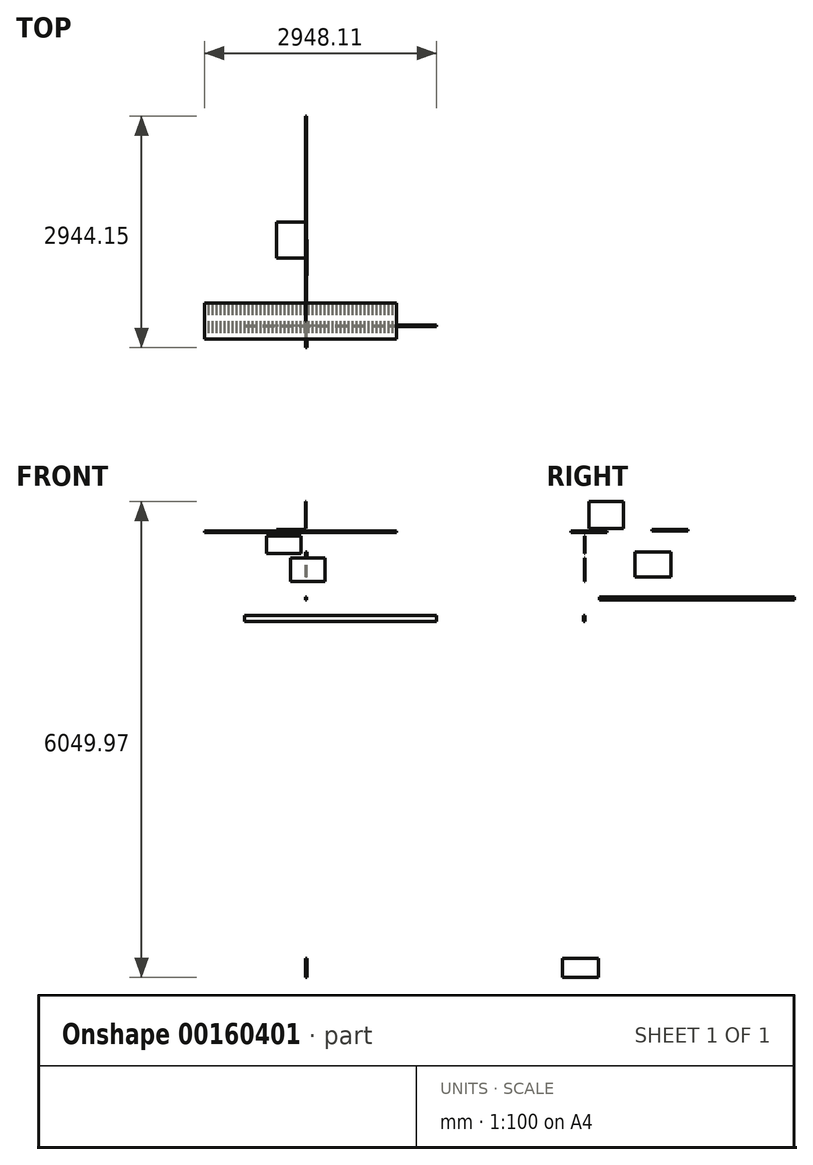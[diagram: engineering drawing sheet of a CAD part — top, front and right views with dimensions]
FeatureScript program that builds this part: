
annotation { "Feature Type Name" : "Feature", "Feature Type Description" : "" }
export const myFeature = defineFeature(function(context is Context, id is Id, definition is map)
    precondition{}
    {
        {
            var Q0;
            Q0=qCreatedBy(makeId("Top.planeOp"),FACE);
            var sketch = newSketch(context, id + "F0", { "sketchPlane" : qUnion([Q0])});
            skLineSegment(sketch, "E0.bottom", {"start": v(-1285.12, 279.2) * mm, "end": v(1153.28, 279.2) * mm});
            skLineSegment(sketch, "E0.top", {"start": v(-1285.12, -178) * mm, "end": v(1153.28, -178) * mm});
            skLineSegment(sketch, "E0.left", {"start": v(-1285.12, 279.2) * mm, "end": v(-1285.12, -178) * mm});
            skLineSegment(sketch, "E0.right", {"start": v(1153.28, 279.2) * mm, "end": v(1153.28, -178) * mm});
            skLineSegment(sketch, "E1.0", {"start": v(-1237.5, 279.2) * mm, "end": v(-1237.5, -178) * mm});
            skLineSegment(sketch, "E2.0", {"start": v(-1231.15, 279.2) * mm, "end": v(-1231.15, -178) * mm});
            skLineSegment(sketch, "E3.1.0.0", {"start": v(-1180.35, 279.2) * mm, "end": v(-1180.35, -178) * mm});
            skLineSegment(sketch, "E3.1.0.1", {"start": v(-1186.7, 279.2) * mm, "end": v(-1186.7, -178) * mm});
            skLineSegment(sketch, "E3.2.0.0", {"start": v(-1129.55, 279.2) * mm, "end": v(-1129.55, -178) * mm});
            skLineSegment(sketch, "E3.2.0.1", {"start": v(-1135.9, 279.2) * mm, "end": v(-1135.9, -178) * mm});
            skLineSegment(sketch, "E3.3.0.0", {"start": v(-1078.75, 279.2) * mm, "end": v(-1078.75, -178) * mm});
            skLineSegment(sketch, "E3.3.0.1", {"start": v(-1085.1, 279.2) * mm, "end": v(-1085.1, -178) * mm});
            skLineSegment(sketch, "E3.4.0.0", {"start": v(-1027.95, 279.2) * mm, "end": v(-1027.95, -178) * mm});
            skLineSegment(sketch, "E3.4.0.1", {"start": v(-1034.3, 279.2) * mm, "end": v(-1034.3, -178) * mm});
            skLineSegment(sketch, "E3.5.0.0", {"start": v(-977.15, 279.2) * mm, "end": v(-977.15, -178) * mm});
            skLineSegment(sketch, "E3.5.0.1", {"start": v(-983.5, 279.2) * mm, "end": v(-983.5, -178) * mm});
            skLineSegment(sketch, "E3.6.0.0", {"start": v(-926.35, 279.2) * mm, "end": v(-926.35, -178) * mm});
            skLineSegment(sketch, "E3.6.0.1", {"start": v(-932.7, 279.2) * mm, "end": v(-932.7, -178) * mm});
            skLineSegment(sketch, "E3.7.0.0", {"start": v(-875.55, 279.2) * mm, "end": v(-875.55, -178) * mm});
            skLineSegment(sketch, "E3.7.0.1", {"start": v(-881.9, 279.2) * mm, "end": v(-881.9, -178) * mm});
            skLineSegment(sketch, "E3.8.0.0", {"start": v(-824.75, 279.2) * mm, "end": v(-824.75, -178) * mm});
            skLineSegment(sketch, "E3.8.0.1", {"start": v(-831.1, 279.2) * mm, "end": v(-831.1, -178) * mm});
            skLineSegment(sketch, "E3.9.0.0", {"start": v(-773.95, 279.2) * mm, "end": v(-773.95, -178) * mm});
            skLineSegment(sketch, "E3.9.0.1", {"start": v(-780.3, 279.2) * mm, "end": v(-780.3, -178) * mm});
            skLineSegment(sketch, "E3.10.0.0", {"start": v(-723.15, 279.2) * mm, "end": v(-723.15, -178) * mm});
            skLineSegment(sketch, "E3.10.0.1", {"start": v(-729.5, 279.2) * mm, "end": v(-729.5, -178) * mm});
            skLineSegment(sketch, "E3.11.0.0", {"start": v(-672.35, 279.2) * mm, "end": v(-672.35, -178) * mm});
            skLineSegment(sketch, "E3.11.0.1", {"start": v(-678.7, 279.2) * mm, "end": v(-678.7, -178) * mm});
            skLineSegment(sketch, "E3.12.0.0", {"start": v(-621.55, 279.2) * mm, "end": v(-621.55, -178) * mm});
            skLineSegment(sketch, "E3.12.0.1", {"start": v(-627.9, 279.2) * mm, "end": v(-627.9, -178) * mm});
            skLineSegment(sketch, "E3.13.0.0", {"start": v(-570.75, 279.2) * mm, "end": v(-570.75, -178) * mm});
            skLineSegment(sketch, "E3.13.0.1", {"start": v(-577.1, 279.2) * mm, "end": v(-577.1, -178) * mm});
            skLineSegment(sketch, "E3.14.0.0", {"start": v(-519.95, 279.2) * mm, "end": v(-519.95, -178) * mm});
            skLineSegment(sketch, "E3.14.0.1", {"start": v(-526.3, 279.2) * mm, "end": v(-526.3, -178) * mm});
            skLineSegment(sketch, "E3.15.0.0", {"start": v(-469.15, 279.2) * mm, "end": v(-469.15, -178) * mm});
            skLineSegment(sketch, "E3.15.0.1", {"start": v(-475.5, 279.2) * mm, "end": v(-475.5, -178) * mm});
            skLineSegment(sketch, "E3.16.0.0", {"start": v(-418.35, 279.2) * mm, "end": v(-418.35, -178) * mm});
            skLineSegment(sketch, "E3.16.0.1", {"start": v(-424.7, 279.2) * mm, "end": v(-424.7, -178) * mm});
            skLineSegment(sketch, "E3.17.0.0", {"start": v(-367.55, 279.2) * mm, "end": v(-367.55, -178) * mm});
            skLineSegment(sketch, "E3.17.0.1", {"start": v(-373.9, 279.2) * mm, "end": v(-373.9, -178) * mm});
            skLineSegment(sketch, "E3.18.0.0", {"start": v(-316.75, 279.2) * mm, "end": v(-316.75, -178) * mm});
            skLineSegment(sketch, "E3.18.0.1", {"start": v(-323.1, 279.2) * mm, "end": v(-323.1, -178) * mm});
            skLineSegment(sketch, "E3.19.0.0", {"start": v(-265.95, 279.2) * mm, "end": v(-265.95, -178) * mm});
            skLineSegment(sketch, "E3.19.0.1", {"start": v(-272.3, 279.2) * mm, "end": v(-272.3, -178) * mm});
            skLineSegment(sketch, "E3.20.0.0", {"start": v(-215.15, 279.2) * mm, "end": v(-215.15, -178) * mm});
            skLineSegment(sketch, "E3.20.0.1", {"start": v(-221.5, 279.2) * mm, "end": v(-221.5, -178) * mm});
            skLineSegment(sketch, "E3.21.0.0", {"start": v(-164.35, 279.2) * mm, "end": v(-164.35, -178) * mm});
            skLineSegment(sketch, "E3.21.0.1", {"start": v(-170.7, 279.2) * mm, "end": v(-170.7, -178) * mm});
            skLineSegment(sketch, "E3.22.0.0", {"start": v(-113.55, 279.2) * mm, "end": v(-113.55, -178) * mm});
            skLineSegment(sketch, "E3.22.0.1", {"start": v(-119.9, 279.2) * mm, "end": v(-119.9, -178) * mm});
            skLineSegment(sketch, "E3.23.0.0", {"start": v(-62.75, 279.2) * mm, "end": v(-62.75, -178) * mm});
            skLineSegment(sketch, "E3.23.0.1", {"start": v(-69.1, 279.2) * mm, "end": v(-69.1, -178) * mm});
            skLineSegment(sketch, "E3.24.0.0", {"start": v(-11.95, 279.2) * mm, "end": v(-11.95, -178) * mm});
            skLineSegment(sketch, "E3.24.0.1", {"start": v(-18.3, 279.2) * mm, "end": v(-18.3, -178) * mm});
            skLineSegment(sketch, "E3.25.0.0", {"start": v(38.85, 279.2) * mm, "end": v(38.85, -178) * mm});
            skLineSegment(sketch, "E3.25.0.1", {"start": v(32.5, 279.2) * mm, "end": v(32.5, -178) * mm});
            skLineSegment(sketch, "E3.26.0.0", {"start": v(89.65, 279.2) * mm, "end": v(89.65, -178) * mm});
            skLineSegment(sketch, "E3.26.0.1", {"start": v(83.3, 279.2) * mm, "end": v(83.3, -178) * mm});
            skLineSegment(sketch, "E3.27.0.0", {"start": v(140.45, 279.2) * mm, "end": v(140.45, -178) * mm});
            skLineSegment(sketch, "E3.27.0.1", {"start": v(134.1, 279.2) * mm, "end": v(134.1, -178) * mm});
            skLineSegment(sketch, "E3.28.0.0", {"start": v(191.25, 279.2) * mm, "end": v(191.25, -178) * mm});
            skLineSegment(sketch, "E3.28.0.1", {"start": v(184.9, 279.2) * mm, "end": v(184.9, -178) * mm});
            skLineSegment(sketch, "E3.29.0.0", {"start": v(242.05, 279.2) * mm, "end": v(242.05, -178) * mm});
            skLineSegment(sketch, "E3.29.0.1", {"start": v(235.7, 279.2) * mm, "end": v(235.7, -178) * mm});
            skLineSegment(sketch, "E3.30.0.0", {"start": v(292.85, 279.2) * mm, "end": v(292.85, -178) * mm});
            skLineSegment(sketch, "E3.30.0.1", {"start": v(286.5, 279.2) * mm, "end": v(286.5, -178) * mm});
            skLineSegment(sketch, "E3.31.0.0", {"start": v(343.65, 279.2) * mm, "end": v(343.65, -178) * mm});
            skLineSegment(sketch, "E3.31.0.1", {"start": v(337.3, 279.2) * mm, "end": v(337.3, -178) * mm});
            skLineSegment(sketch, "E3.32.0.0", {"start": v(394.45, 279.2) * mm, "end": v(394.45, -178) * mm});
            skLineSegment(sketch, "E3.32.0.1", {"start": v(388.1, 279.2) * mm, "end": v(388.1, -178) * mm});
            skLineSegment(sketch, "E3.33.0.0", {"start": v(445.25, 279.2) * mm, "end": v(445.25, -178) * mm});
            skLineSegment(sketch, "E3.33.0.1", {"start": v(438.9, 279.2) * mm, "end": v(438.9, -178) * mm});
            skLineSegment(sketch, "E3.34.0.0", {"start": v(496.05, 279.2) * mm, "end": v(496.05, -178) * mm});
            skLineSegment(sketch, "E3.34.0.1", {"start": v(489.7, 279.2) * mm, "end": v(489.7, -178) * mm});
            skLineSegment(sketch, "E3.35.0.0", {"start": v(546.85, 279.2) * mm, "end": v(546.85, -178) * mm});
            skLineSegment(sketch, "E3.35.0.1", {"start": v(540.5, 279.2) * mm, "end": v(540.5, -178) * mm});
            skLineSegment(sketch, "E3.36.0.0", {"start": v(597.65, 279.2) * mm, "end": v(597.65, -178) * mm});
            skLineSegment(sketch, "E3.36.0.1", {"start": v(591.3, 279.2) * mm, "end": v(591.3, -178) * mm});
            skLineSegment(sketch, "E3.37.0.0", {"start": v(648.45, 279.2) * mm, "end": v(648.45, -178) * mm});
            skLineSegment(sketch, "E3.37.0.1", {"start": v(642.1, 279.2) * mm, "end": v(642.1, -178) * mm});
            skLineSegment(sketch, "E3.38.0.0", {"start": v(699.25, 279.2) * mm, "end": v(699.25, -178) * mm});
            skLineSegment(sketch, "E3.38.0.1", {"start": v(692.9, 279.2) * mm, "end": v(692.9, -178) * mm});
            skLineSegment(sketch, "E3.39.0.0", {"start": v(750.05, 279.2) * mm, "end": v(750.05, -178) * mm});
            skLineSegment(sketch, "E3.39.0.1", {"start": v(743.7, 279.2) * mm, "end": v(743.7, -178) * mm});
            skLineSegment(sketch, "E3.40.0.0", {"start": v(800.85, 279.2) * mm, "end": v(800.85, -178) * mm});
            skLineSegment(sketch, "E3.40.0.1", {"start": v(794.5, 279.2) * mm, "end": v(794.5, -178) * mm});
            skLineSegment(sketch, "E3.41.0.0", {"start": v(851.65, 279.2) * mm, "end": v(851.65, -178) * mm});
            skLineSegment(sketch, "E3.41.0.1", {"start": v(845.3, 279.2) * mm, "end": v(845.3, -178) * mm});
            skLineSegment(sketch, "E3.42.0.0", {"start": v(902.45, 279.2) * mm, "end": v(902.45, -178) * mm});
            skLineSegment(sketch, "E3.42.0.1", {"start": v(896.1, 279.2) * mm, "end": v(896.1, -178) * mm});
            skLineSegment(sketch, "E3.43.0.0", {"start": v(953.25, 279.2) * mm, "end": v(953.25, -178) * mm});
            skLineSegment(sketch, "E3.43.0.1", {"start": v(946.9, 279.2) * mm, "end": v(946.9, -178) * mm});
            skLineSegment(sketch, "E3.44.0.0", {"start": v(1004.05, 279.2) * mm, "end": v(1004.05, -178) * mm});
            skLineSegment(sketch, "E3.44.0.1", {"start": v(997.7, 279.2) * mm, "end": v(997.7, -178) * mm});
            skLineSegment(sketch, "E3.45.0.0", {"start": v(1054.85, 279.2) * mm, "end": v(1054.85, -178) * mm});
            skLineSegment(sketch, "E3.45.0.1", {"start": v(1048.5, 279.2) * mm, "end": v(1048.5, -178) * mm});
            skLineSegment(sketch, "E3.46.0.0", {"start": v(1105.65, 279.2) * mm, "end": v(1105.65, -178) * mm});
            skLineSegment(sketch, "E3.46.0.1", {"start": v(1099.3, 279.2) * mm, "end": v(1099.3, -178) * mm});
            skLineSegment(sketch, "E3.direction1", {"start": v(-1237.5, -178) * mm, "end": v(-1186.7, -178) * mm, "construction": true});
            skSolve(sketch);
        }
        {
            var Q0;
            Q0 = qSketchRegion(id + "F0", true);
            extrude(context, id + "F1", {"entities" : qUnion([Q0]), "depth" : 19.05 * mm});
        }
        {
            var Q0;
            {var subQ0=sQuery(id+"F0.wireOp",EDGE,"E1.0");Q0=makeQuery(id+"F0.imprint","IMPRINT",FACE,{"disambiguationData":[TD([[makeQuery(id+"F0.imprint","IMPRINT",EDGE,{"derivedFrom":subQ0}),1.0]])]});}
            var Q1;
            {var subQ0=sQuery(id+"F0.wireOp",EDGE,"E3.1.0.0");Q1=makeQuery(id+"F0.imprint","IMPRINT",FACE,{"disambiguationData":[TD([[makeQuery(id+"F0.imprint","IMPRINT",EDGE,{"derivedFrom":subQ0}),-1.0]])]});}
            var Q2;
            {var subQ0=sQuery(id+"F0.wireOp",EDGE,"E3.2.0.0");Q2=makeQuery(id+"F0.imprint","IMPRINT",FACE,{"disambiguationData":[TD([[makeQuery(id+"F0.imprint","IMPRINT",EDGE,{"derivedFrom":subQ0}),-1.0]])]});}
            var Q3;
            {var subQ0=sQuery(id+"F0.wireOp",EDGE,"E3.3.0.0");Q3=makeQuery(id+"F0.imprint","IMPRINT",FACE,{"disambiguationData":[TD([[makeQuery(id+"F0.imprint","IMPRINT",EDGE,{"derivedFrom":subQ0}),-1.0]])]});}
            var Q4;
            {var subQ0=sQuery(id+"F0.wireOp",EDGE,"E3.4.0.0");Q4=makeQuery(id+"F0.imprint","IMPRINT",FACE,{"disambiguationData":[TD([[makeQuery(id+"F0.imprint","IMPRINT",EDGE,{"derivedFrom":subQ0}),-1.0]])]});}
            var Q5;
            {var subQ0=sQuery(id+"F0.wireOp",EDGE,"E3.5.0.0");Q5=makeQuery(id+"F0.imprint","IMPRINT",FACE,{"disambiguationData":[TD([[makeQuery(id+"F0.imprint","IMPRINT",EDGE,{"derivedFrom":subQ0}),-1.0]])]});}
            var Q6;
            {var subQ0=sQuery(id+"F0.wireOp",EDGE,"E3.6.0.0");Q6=makeQuery(id+"F0.imprint","IMPRINT",FACE,{"disambiguationData":[TD([[makeQuery(id+"F0.imprint","IMPRINT",EDGE,{"derivedFrom":subQ0}),-1.0]])]});}
            var Q7;
            {var subQ0=sQuery(id+"F0.wireOp",EDGE,"E3.7.0.0");Q7=makeQuery(id+"F0.imprint","IMPRINT",FACE,{"disambiguationData":[TD([[makeQuery(id+"F0.imprint","IMPRINT",EDGE,{"derivedFrom":subQ0}),-1.0]])]});}
            var Q8;
            {var subQ0=sQuery(id+"F0.wireOp",EDGE,"E3.8.0.0");Q8=makeQuery(id+"F0.imprint","IMPRINT",FACE,{"disambiguationData":[TD([[makeQuery(id+"F0.imprint","IMPRINT",EDGE,{"derivedFrom":subQ0}),-1.0]])]});}
            var Q9;
            {var subQ0=sQuery(id+"F0.wireOp",EDGE,"E3.9.0.0");Q9=makeQuery(id+"F0.imprint","IMPRINT",FACE,{"disambiguationData":[TD([[makeQuery(id+"F0.imprint","IMPRINT",EDGE,{"derivedFrom":subQ0}),-1.0]])]});}
            var Q10;
            {var subQ0=sQuery(id+"F0.wireOp",EDGE,"E3.10.0.0");Q10=makeQuery(id+"F0.imprint","IMPRINT",FACE,{"disambiguationData":[TD([[makeQuery(id+"F0.imprint","IMPRINT",EDGE,{"derivedFrom":subQ0}),-1.0]])]});}
            var Q11;
            {var subQ0=sQuery(id+"F0.wireOp",EDGE,"E3.11.0.0");Q11=makeQuery(id+"F0.imprint","IMPRINT",FACE,{"disambiguationData":[TD([[makeQuery(id+"F0.imprint","IMPRINT",EDGE,{"derivedFrom":subQ0}),-1.0]])]});}
            var Q12;
            {var subQ0=sQuery(id+"F0.wireOp",EDGE,"E3.12.0.0");Q12=makeQuery(id+"F0.imprint","IMPRINT",FACE,{"disambiguationData":[TD([[makeQuery(id+"F0.imprint","IMPRINT",EDGE,{"derivedFrom":subQ0}),-1.0]])]});}
            var Q13;
            {var subQ0=sQuery(id+"F0.wireOp",EDGE,"E3.13.0.0");Q13=makeQuery(id+"F0.imprint","IMPRINT",FACE,{"disambiguationData":[TD([[makeQuery(id+"F0.imprint","IMPRINT",EDGE,{"derivedFrom":subQ0}),-1.0]])]});}
            var Q14;
            {var subQ0=sQuery(id+"F0.wireOp",EDGE,"E3.14.0.0");Q14=makeQuery(id+"F0.imprint","IMPRINT",FACE,{"disambiguationData":[TD([[makeQuery(id+"F0.imprint","IMPRINT",EDGE,{"derivedFrom":subQ0}),-1.0]])]});}
            var Q15;
            {var subQ0=sQuery(id+"F0.wireOp",EDGE,"E3.15.0.0");Q15=makeQuery(id+"F0.imprint","IMPRINT",FACE,{"disambiguationData":[TD([[makeQuery(id+"F0.imprint","IMPRINT",EDGE,{"derivedFrom":subQ0}),-1.0]])]});}
            var Q16;
            {var subQ0=sQuery(id+"F0.wireOp",EDGE,"E3.16.0.0");Q16=makeQuery(id+"F0.imprint","IMPRINT",FACE,{"disambiguationData":[TD([[makeQuery(id+"F0.imprint","IMPRINT",EDGE,{"derivedFrom":subQ0}),-1.0]])]});}
            var Q17;
            {var subQ0=sQuery(id+"F0.wireOp",EDGE,"E3.17.0.0");Q17=makeQuery(id+"F0.imprint","IMPRINT",FACE,{"disambiguationData":[TD([[makeQuery(id+"F0.imprint","IMPRINT",EDGE,{"derivedFrom":subQ0}),-1.0]])]});}
            var Q18;
            {var subQ0=sQuery(id+"F0.wireOp",EDGE,"E3.18.0.0");Q18=makeQuery(id+"F0.imprint","IMPRINT",FACE,{"disambiguationData":[TD([[makeQuery(id+"F0.imprint","IMPRINT",EDGE,{"derivedFrom":subQ0}),-1.0]])]});}
            var Q19;
            {var subQ0=sQuery(id+"F0.wireOp",EDGE,"E3.19.0.0");Q19=makeQuery(id+"F0.imprint","IMPRINT",FACE,{"disambiguationData":[TD([[makeQuery(id+"F0.imprint","IMPRINT",EDGE,{"derivedFrom":subQ0}),-1.0]])]});}
            var Q20;
            {var subQ0=sQuery(id+"F0.wireOp",EDGE,"E3.20.0.0");Q20=makeQuery(id+"F0.imprint","IMPRINT",FACE,{"disambiguationData":[TD([[makeQuery(id+"F0.imprint","IMPRINT",EDGE,{"derivedFrom":subQ0}),-1.0]])]});}
            var Q21;
            {var subQ0=sQuery(id+"F0.wireOp",EDGE,"E3.21.0.0");Q21=makeQuery(id+"F0.imprint","IMPRINT",FACE,{"disambiguationData":[TD([[makeQuery(id+"F0.imprint","IMPRINT",EDGE,{"derivedFrom":subQ0}),-1.0]])]});}
            var Q22;
            {var subQ0=sQuery(id+"F0.wireOp",EDGE,"E3.22.0.0");Q22=makeQuery(id+"F0.imprint","IMPRINT",FACE,{"disambiguationData":[TD([[makeQuery(id+"F0.imprint","IMPRINT",EDGE,{"derivedFrom":subQ0}),-1.0]])]});}
            var Q23;
            {var subQ0=sQuery(id+"F0.wireOp",EDGE,"E3.23.0.0");Q23=makeQuery(id+"F0.imprint","IMPRINT",FACE,{"disambiguationData":[TD([[makeQuery(id+"F0.imprint","IMPRINT",EDGE,{"derivedFrom":subQ0}),-1.0]])]});}
            var Q24;
            {var subQ0=sQuery(id+"F0.wireOp",EDGE,"E3.24.0.0");Q24=makeQuery(id+"F0.imprint","IMPRINT",FACE,{"disambiguationData":[TD([[makeQuery(id+"F0.imprint","IMPRINT",EDGE,{"derivedFrom":subQ0}),-1.0]])]});}
            var Q25;
            {var subQ0=sQuery(id+"F0.wireOp",EDGE,"E3.25.0.0");Q25=makeQuery(id+"F0.imprint","IMPRINT",FACE,{"disambiguationData":[TD([[makeQuery(id+"F0.imprint","IMPRINT",EDGE,{"derivedFrom":subQ0}),-1.0]])]});}
            var Q26;
            {var subQ0=sQuery(id+"F0.wireOp",EDGE,"E3.26.0.0");Q26=makeQuery(id+"F0.imprint","IMPRINT",FACE,{"disambiguationData":[TD([[makeQuery(id+"F0.imprint","IMPRINT",EDGE,{"derivedFrom":subQ0}),-1.0]])]});}
            var Q27;
            {var subQ0=sQuery(id+"F0.wireOp",EDGE,"E3.27.0.0");Q27=makeQuery(id+"F0.imprint","IMPRINT",FACE,{"disambiguationData":[TD([[makeQuery(id+"F0.imprint","IMPRINT",EDGE,{"derivedFrom":subQ0}),-1.0]])]});}
            var Q28;
            {var subQ0=sQuery(id+"F0.wireOp",EDGE,"E3.28.0.0");Q28=makeQuery(id+"F0.imprint","IMPRINT",FACE,{"disambiguationData":[TD([[makeQuery(id+"F0.imprint","IMPRINT",EDGE,{"derivedFrom":subQ0}),-1.0]])]});}
            var Q29;
            {var subQ0=sQuery(id+"F0.wireOp",EDGE,"E3.29.0.0");Q29=makeQuery(id+"F0.imprint","IMPRINT",FACE,{"disambiguationData":[TD([[makeQuery(id+"F0.imprint","IMPRINT",EDGE,{"derivedFrom":subQ0}),-1.0]])]});}
            var Q30;
            {var subQ0=sQuery(id+"F0.wireOp",EDGE,"E3.30.0.0");Q30=makeQuery(id+"F0.imprint","IMPRINT",FACE,{"disambiguationData":[TD([[makeQuery(id+"F0.imprint","IMPRINT",EDGE,{"derivedFrom":subQ0}),-1.0]])]});}
            var Q31;
            {var subQ0=sQuery(id+"F0.wireOp",EDGE,"E3.31.0.0");Q31=makeQuery(id+"F0.imprint","IMPRINT",FACE,{"disambiguationData":[TD([[makeQuery(id+"F0.imprint","IMPRINT",EDGE,{"derivedFrom":subQ0}),-1.0]])]});}
            var Q32;
            {var subQ0=sQuery(id+"F0.wireOp",EDGE,"E3.32.0.0");Q32=makeQuery(id+"F0.imprint","IMPRINT",FACE,{"disambiguationData":[TD([[makeQuery(id+"F0.imprint","IMPRINT",EDGE,{"derivedFrom":subQ0}),-1.0]])]});}
            var Q33;
            {var subQ0=sQuery(id+"F0.wireOp",EDGE,"E3.33.0.0");Q33=makeQuery(id+"F0.imprint","IMPRINT",FACE,{"disambiguationData":[TD([[makeQuery(id+"F0.imprint","IMPRINT",EDGE,{"derivedFrom":subQ0}),-1.0]])]});}
            var Q34;
            {var subQ0=sQuery(id+"F0.wireOp",EDGE,"E3.34.0.0");Q34=makeQuery(id+"F0.imprint","IMPRINT",FACE,{"disambiguationData":[TD([[makeQuery(id+"F0.imprint","IMPRINT",EDGE,{"derivedFrom":subQ0}),-1.0]])]});}
            var Q35;
            {var subQ0=sQuery(id+"F0.wireOp",EDGE,"E3.35.0.0");Q35=makeQuery(id+"F0.imprint","IMPRINT",FACE,{"disambiguationData":[TD([[makeQuery(id+"F0.imprint","IMPRINT",EDGE,{"derivedFrom":subQ0}),-1.0]])]});}
            var Q36;
            {var subQ0=sQuery(id+"F0.wireOp",EDGE,"E3.36.0.0");Q36=makeQuery(id+"F0.imprint","IMPRINT",FACE,{"disambiguationData":[TD([[makeQuery(id+"F0.imprint","IMPRINT",EDGE,{"derivedFrom":subQ0}),-1.0]])]});}
            var Q37;
            {var subQ0=sQuery(id+"F0.wireOp",EDGE,"E3.37.0.0");Q37=makeQuery(id+"F0.imprint","IMPRINT",FACE,{"disambiguationData":[TD([[makeQuery(id+"F0.imprint","IMPRINT",EDGE,{"derivedFrom":subQ0}),-1.0]])]});}
            var Q38;
            {var subQ0=sQuery(id+"F0.wireOp",EDGE,"E3.38.0.0");Q38=makeQuery(id+"F0.imprint","IMPRINT",FACE,{"disambiguationData":[TD([[makeQuery(id+"F0.imprint","IMPRINT",EDGE,{"derivedFrom":subQ0}),-1.0]])]});}
            var Q39;
            {var subQ0=sQuery(id+"F0.wireOp",EDGE,"E3.39.0.0");Q39=makeQuery(id+"F0.imprint","IMPRINT",FACE,{"disambiguationData":[TD([[makeQuery(id+"F0.imprint","IMPRINT",EDGE,{"derivedFrom":subQ0}),-1.0]])]});}
            var Q40;
            {var subQ0=sQuery(id+"F0.wireOp",EDGE,"E3.40.0.0");Q40=makeQuery(id+"F0.imprint","IMPRINT",FACE,{"disambiguationData":[TD([[makeQuery(id+"F0.imprint","IMPRINT",EDGE,{"derivedFrom":subQ0}),-1.0]])]});}
            var Q41;
            {var subQ0=sQuery(id+"F0.wireOp",EDGE,"E3.41.0.0");Q41=makeQuery(id+"F0.imprint","IMPRINT",FACE,{"disambiguationData":[TD([[makeQuery(id+"F0.imprint","IMPRINT",EDGE,{"derivedFrom":subQ0}),-1.0]])]});}
            var Q42;
            {var subQ0=sQuery(id+"F0.wireOp",EDGE,"E3.42.0.0");Q42=makeQuery(id+"F0.imprint","IMPRINT",FACE,{"disambiguationData":[TD([[makeQuery(id+"F0.imprint","IMPRINT",EDGE,{"derivedFrom":subQ0}),-1.0]])]});}
            var Q43;
            {var subQ0=sQuery(id+"F0.wireOp",EDGE,"E3.43.0.0");Q43=makeQuery(id+"F0.imprint","IMPRINT",FACE,{"disambiguationData":[TD([[makeQuery(id+"F0.imprint","IMPRINT",EDGE,{"derivedFrom":subQ0}),-1.0]])]});}
            var Q44;
            {var subQ0=sQuery(id+"F0.wireOp",EDGE,"E3.44.0.0");Q44=makeQuery(id+"F0.imprint","IMPRINT",FACE,{"disambiguationData":[TD([[makeQuery(id+"F0.imprint","IMPRINT",EDGE,{"derivedFrom":subQ0}),-1.0]])]});}
            var Q45;
            {var subQ0=sQuery(id+"F0.wireOp",EDGE,"E3.45.0.0");Q45=makeQuery(id+"F0.imprint","IMPRINT",FACE,{"disambiguationData":[TD([[makeQuery(id+"F0.imprint","IMPRINT",EDGE,{"derivedFrom":subQ0}),-1.0]])]});}
            var Q46;
            {var subQ0=sQuery(id+"F0.wireOp",EDGE,"E3.46.0.0");Q46=makeQuery(id+"F0.imprint","IMPRINT",FACE,{"disambiguationData":[TD([[makeQuery(id+"F0.imprint","IMPRINT",EDGE,{"derivedFrom":subQ0}),-1.0]])]});}
            extrude(context, id + "F2", {"entities" : qUnion([Q0, Q1, Q2, Q3, Q4, Q5, Q6, Q7, Q8, Q9, Q10, Q11, Q12, Q13, Q14, Q15, Q16, Q17, Q18, Q19, Q20, Q21, Q22, Q23, Q24, Q25, Q26, Q27, Q28, Q29, Q30, Q31, Q32, Q33, Q34, Q35, Q36, Q37, Q38, Q39, Q40, Q41, Q42, Q43, Q44, Q45, Q46]), "operationType" : NewBodyOperationType.REMOVE, "depth" : 8.25 * mm});
        }
        {
            var Q0;
            Q0=makeQuery(id+"F1.opExtrude","CAP_FACE",FACE,{"disambiguationData":[OSD([sQuery(id+"F0.wireOp",EDGE,"E0.bottom"),sQuery(id+"F0.wireOp",EDGE,"E0.top"),sQuery(id+"F0.wireOp",EDGE,"E0.left"),sQuery(id+"F0.wireOp",EDGE,"E0.right")])],"isStart":false});
            var sketch = newSketch(context, id + "F3", { "sketchPlane" : qUnion([Q0])});
            skLineSegment(sketch, "E4.bottom", {"start": v(-368.3, 851.06) * mm, "end": v(0, 851.06) * mm});
            skLineSegment(sketch, "E4.top", {"start": v(-368.3, 1308.26) * mm, "end": v(0, 1308.26) * mm});
            skLineSegment(sketch, "E4.left", {"start": v(-368.3, 851.06) * mm, "end": v(-368.3, 1308.26) * mm});
            skLineSegment(sketch, "E4.right", {"start": v(0, 851.06) * mm, "end": v(0, 1308.26) * mm});
            skSolve(sketch);
        }
        {
            var Q0;
            Q0 = qSketchRegion(id + "F3", true);
            extrude(context, id + "F4", {"entities" : qUnion([Q0]), "depth" : 19.05 * mm});
        }
        {
            var Q0;
            Q0=qCreatedBy(makeId("Right.planeOp"),FACE);
            var sketch = newSketch(context, id + "F5", { "sketchPlane" : qUnion([Q0])});
            skLineSegment(sketch, "E5.bottom", {"start": v(-288.3, -5413.9) * mm, "end": v(168.9, -5413.9) * mm});
            skLineSegment(sketch, "E5.top", {"start": v(-288.3, -5655.2) * mm, "end": v(168.9, -5655.2) * mm});
            skLineSegment(sketch, "E5.left", {"start": v(-288.3, -5413.9) * mm, "end": v(-288.3, -5655.2) * mm});
            skLineSegment(sketch, "E5.right", {"start": v(168.9, -5413.9) * mm, "end": v(168.9, -5655.2) * mm});
            skSolve(sketch);
        }
        {
            var Q0;
            Q0 = qSketchRegion(id + "F5", true);
            extrude(context, id + "F6", {"entities" : qUnion([Q0]), "depth" : 19.05 * mm});
        }
        {
            var Q0;
            Q0=qCreatedBy(makeId("Right.planeOp"),FACE);
            var sketch = newSketch(context, id + "F7", { "sketchPlane" : qUnion([Q0])});
            skLineSegment(sketch, "E6.bottom", {"start": v(487.95, 48.7) * mm, "end": v(49.8, 48.7) * mm});
            skLineSegment(sketch, "E6.top", {"start": v(487.95, 394.78) * mm, "end": v(49.8, 394.78) * mm});
            skLineSegment(sketch, "E6.left", {"start": v(487.95, 48.7) * mm, "end": v(487.95, 394.78) * mm});
            skLineSegment(sketch, "E6.right", {"start": v(49.8, 48.7) * mm, "end": v(49.8, 394.78) * mm});
            skSolve(sketch);
        }
        {
            var Q0;
            Q0 = qSketchRegion(id + "F7", true);
            extrude(context, id + "F8", {"entities" : qUnion([Q0]), "depth" : 6.35 * mm});
        }
        {
            var Q0;
            Q0=qCreatedBy(makeId("Front.planeOp"),FACE);
            var sketch = newSketch(context, id + "F9", { "sketchPlane" : qUnion([Q0])});
            skLineSegment(sketch, "E7.bottom", {"start": v(-496.15, -267.26) * mm, "end": v(-58, -267.26) * mm});
            skLineSegment(sketch, "E7.top", {"start": v(-496.15, -48.18) * mm, "end": v(-58, -48.18) * mm});
            skLineSegment(sketch, "E7.left", {"start": v(-496.15, -267.26) * mm, "end": v(-496.15, -48.18) * mm});
            skLineSegment(sketch, "E7.right", {"start": v(-58, -267.26) * mm, "end": v(-58, -48.18) * mm});
            skSolve(sketch);
        }
        {
            var Q0;
            Q0 = qSketchRegion(id + "F9", true);
            extrude(context, id + "F10", {"entities" : qUnion([Q0]), "depth" : 6.35 * mm});
        }
        {
            var Q0;
            Q0=qCreatedBy(makeId("Front.planeOp"),FACE);
            var sketch = newSketch(context, id + "F11", { "sketchPlane" : qUnion([Q0])});
            skLineSegment(sketch, "E8.bottom", {"start": v(-190.1, -622.26) * mm, "end": v(248.04, -622.26) * mm});
            skLineSegment(sketch, "E8.top", {"start": v(-190.1, -326.98) * mm, "end": v(248.04, -326.98) * mm});
            skLineSegment(sketch, "E8.left", {"start": v(-190.1, -622.26) * mm, "end": v(-190.1, -326.98) * mm});
            skLineSegment(sketch, "E8.right", {"start": v(248.04, -622.26) * mm, "end": v(248.04, -326.98) * mm});
            skSolve(sketch);
        }
        {
            var Q0;
            Q0 = qSketchRegion(id + "F11", true);
            extrude(context, id + "F12", {"entities" : qUnion([Q0]), "depth" : 6.35 * mm});
        }
        {
            var Q0;
            Q0=qCreatedBy(makeId("Front.planeOp"),FACE);
            var sketch = newSketch(context, id + "F13", { "sketchPlane" : qUnion([Q0])});
            skLineSegment(sketch, "E9.bottom", {"start": v(-775.4, -1132.11) * mm, "end": v(1663, -1132.11) * mm});
            skLineSegment(sketch, "E9.top", {"start": v(-775.4, -1055.91) * mm, "end": v(1663, -1055.91) * mm});
            skLineSegment(sketch, "E9.left", {"start": v(-775.4, -1132.11) * mm, "end": v(-775.4, -1055.91) * mm});
            skLineSegment(sketch, "E9.right", {"start": v(1663, -1132.11) * mm, "end": v(1663, -1055.91) * mm});
            skSolve(sketch);
        }
        {
            var Q0;
            Q0 = qSketchRegion(id + "F13", true);
            extrude(context, id + "F14", {"entities" : qUnion([Q0]), "depth" : 19.05 * mm});
        }
        {
            var Q0;
            Q0=qCreatedBy(makeId("Right.planeOp"),FACE);
            var sketch = newSketch(context, id + "F15", { "sketchPlane" : qUnion([Q0])});
            skLineSegment(sketch, "E10.bottom", {"start": v(1089.11, -564) * mm, "end": v(631.91, -564) * mm});
            skLineSegment(sketch, "E10.top", {"start": v(1089.11, -246.5) * mm, "end": v(631.91, -246.5) * mm});
            skLineSegment(sketch, "E10.left", {"start": v(1089.11, -564) * mm, "end": v(1089.11, -246.5) * mm});
            skLineSegment(sketch, "E10.right", {"start": v(631.91, -564) * mm, "end": v(631.91, -246.5) * mm});
            skSolve(sketch);
        }
        {
            var Q0;
            Q0 = qSketchRegion(id + "F15", true);
            extrude(context, id + "F16", {"entities" : qUnion([Q0]), "depth" : 19.05 * mm});
        }
        {
            var Q0;
            Q0=qCreatedBy(makeId("Right.planeOp"),FACE);
            var sketch = newSketch(context, id + "F17", { "sketchPlane" : qUnion([Q0])});
            skLineSegment(sketch, "E11.bottom", {"start": v(2655.85, -860.3) * mm, "end": v(179.35, -860.3) * mm});
            skLineSegment(sketch, "E11.top", {"start": v(2655.85, -822.2) * mm, "end": v(179.35, -822.2) * mm});
            skLineSegment(sketch, "E11.left", {"start": v(2655.85, -860.3) * mm, "end": v(2655.85, -822.2) * mm});
            skLineSegment(sketch, "E11.right", {"start": v(179.35, -860.3) * mm, "end": v(179.35, -822.2) * mm});
            skSolve(sketch);
        }
        {
            var Q0;
            Q0 = qSketchRegion(id + "F17", true);
            extrude(context, id + "F18", {"entities" : qUnion([Q0]), "depth" : 12.7 * mm});
        }
    });
